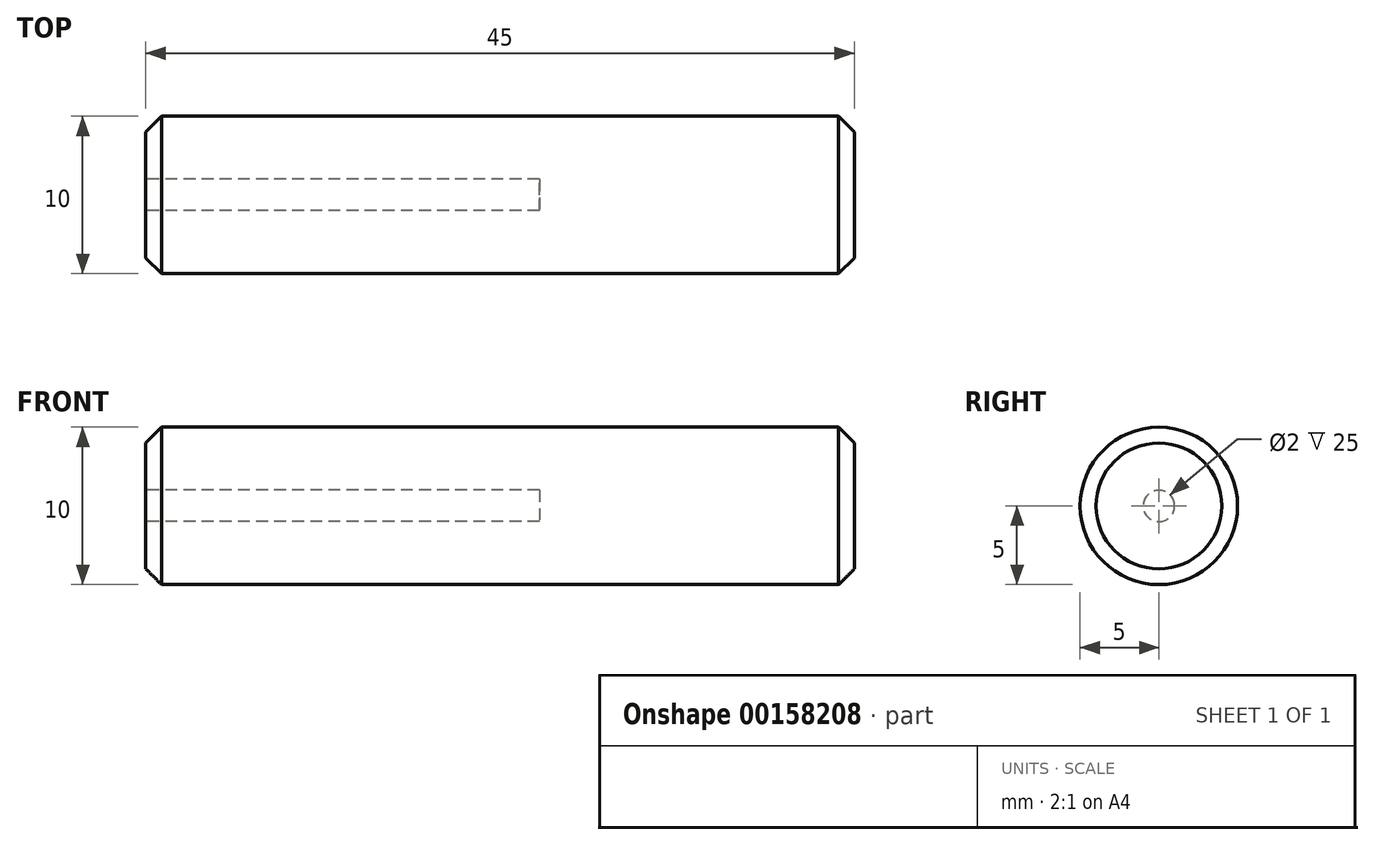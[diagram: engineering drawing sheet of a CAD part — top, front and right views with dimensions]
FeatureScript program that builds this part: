
annotation { "Feature Type Name" : "Feature", "Feature Type Description" : "" }
export const myFeature = defineFeature(function(context is Context, id is Id, definition is map)
    precondition{}
    {
        {
            var Q0;
            Q0=qCreatedBy(makeId("Right.planeOp"),FACE);
            var sketch = newSketch(context, id + "F0", { "sketchPlane" : qUnion([Q0])});
            skCircle(sketch, "E0", {"center": v(0, 0) * mm, "radius": 5 * mm});
            skSolve(sketch);
        }
        {
            var Q0;
            Q0=makeQuery(id+"F0.imprint","IMPRINT",FACE,{"disambiguationData":[TD([[makeQuery(id+"F0.imprint","IMPRINT",EDGE,{"derivedFrom":sQuery(id+"F0.wireOp",EDGE,"E0")}),1.0]])]});
            extrude(context, id + "F1", {"entities" : qUnion([Q0]), "depth" : 45 * mm});
        }
        {
            var Q0;
            Q0=makeQuery(id+"F1.opExtrude","CAP_FACE",FACE,{"disambiguationData":[OSD([sQuery(id+"F0.wireOp",EDGE,"E0")])],"isStart":true});
            var sketch = newSketch(context, id + "F2", { "sketchPlane" : qUnion([Q0])});
            skCircle(sketch, "E1", {"center": v(0, 0) * mm, "radius": 1 * mm});
            skSolve(sketch);
        }
        {
            var Q0;
            Q0=makeQuery(id+"F2.imprint","IMPRINT",FACE,{"disambiguationData":[TD([[makeQuery(id+"F2.imprint","IMPRINT",EDGE,{"derivedFrom":sQuery(id+"F2.wireOp",EDGE,"E1")}),1.0]])]});
            extrude(context, id + "F3", {"entities" : qUnion([Q0]), "operationType" : NewBodyOperationType.REMOVE, "oppositeDirection" : true, "depth" : 25 * mm});
        }
        {
            var Q0;
            Q0=makeQuery(id+"F1.opExtrude","CAP_EDGE",EDGE,{"disambiguationData":[OSD([sQuery(id+"F0.wireOp",EDGE,"E0")])],"isStart":true});
            var Q1;
            Q1=makeQuery(id+"F1.opExtrude","CAP_EDGE",EDGE,{"disambiguationData":[OSD([sQuery(id+"F0.wireOp",EDGE,"E0")])],"isStart":false});
            chamfer(context, id + "F4", {"entities" : qUnion([Q0, Q1]), "width" : 1 * mm, "tangentPropagation" : true});
        }
    });
